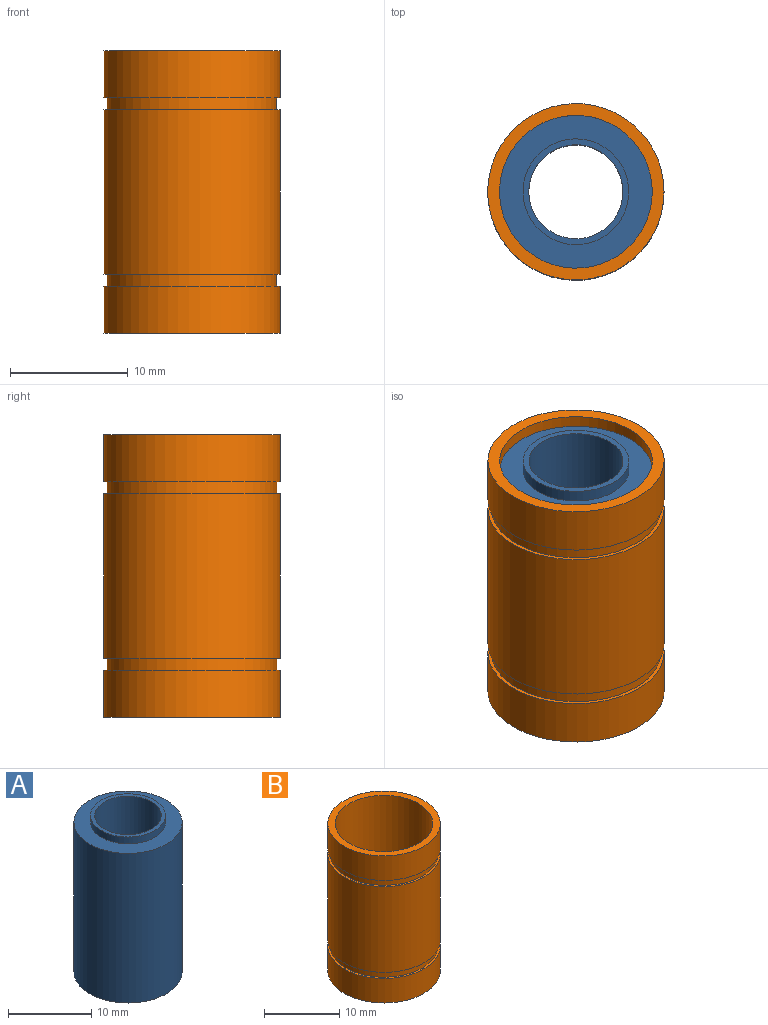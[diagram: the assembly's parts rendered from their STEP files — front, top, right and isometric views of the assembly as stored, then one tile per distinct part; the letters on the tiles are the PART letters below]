
ASSEMBLY  parts=2 mates=1
PART A: 8 faces, bbox 13x13x24 mm
  f0: cylinder r=4.5mm len=9mm, axis (0,0,-1), area 28.3mm2, adj f4,f7
  f1: cylinder r=4mm len=24mm, axis (0,0,-1), area 603.2mm2, adj f3,f4
  f2: cylinder r=4.5mm len=9mm, axis (0,0,-1), area 28.3mm2, adj f3,f6
  f3: plane 9x9mm, normal (0,0,1), area 13.4mm2, adj f1,f2
  f4: plane 9x9mm, normal (0,0,-1), area 13.4mm2, adj f0,f1
  f5: cylinder r=6.5mm len=22mm, axis (0,0,-1), area 898.5mm2, adj f6,f7
  f6: plane 13x13mm, normal (0,0,1), area 69.1mm2, adj f2,f5
  f7: plane 13x13mm, normal (0,0,-1), area 69.1mm2, adj f0,f5
PART B: 12 faces, bbox 15x15x24 mm
  f0: cylinder r=7.5mm len=15mm, axis (0,0,-1), area 188.5mm2, adj f5,f10
  f1: cylinder r=7.5mm len=15mm, axis (0,0,-1), area 659.7mm2, adj f7,f11
  f2: cylinder r=6.5mm len=24mm, axis (0,0,-1), area 980.2mm2, adj f4,f5
  f3: cylinder r=7.5mm len=15mm, axis (0,0,-1), area 188.5mm2, adj f4,f8
  f4: plane 15x15mm, normal (0,0,1), area 44mm2, adj f2,f3
  f5: plane 15x15mm, normal (0,0,-1), area 44mm2, adj f0,f2
  f6: cylinder r=7.2mm len=14.4mm, axis (0,0,1), area 45.2mm2, adj f7,f8
  f7: plane 15x15mm, normal (0,0,1), area 13.9mm2, adj f1,f6
  f8: plane 15x15mm, normal (0,0,-1), area 13.9mm2, adj f3,f6
  f9: cylinder r=7.2mm len=14.4mm, axis (0,0,1), area 45.2mm2, adj f10,f11
  f10: plane 15x15mm, normal (0,0,1), area 13.9mm2, adj f0,f9
  f11: plane 15x15mm, normal (0,0,-1), area 13.9mm2, adj f1,f9
PLACE A t=(19.55,-25.16,8.7)mm
PLACE B t=(19.55,-25.16,8.7)mm
MATE fastened B.f0 <-> A.f0  axis (0,0,1) through (-16.74,4.14,32.7)mm
